FCSTD DOCUMENT  (FreeCAD 0.14R3700 (Git))
Label: 1
License: CC-BY 3.0
LicenseURL: http://creativecommons.org/licenses/by/3.0/
objects: Part::Part2DObjectPython×19
note: 19 computed .brp shape members not serialized (recipe doc carries the construction recipe); baked Part::Feature solids carry a one-line shape summary decoded from their .brp

FEATURE [Part::Part2DObjectPython] Circle  # Draft 2D object (typed FeaturePython)
  FirstAngle = 0
  LastAngle = 0
  MakeFace = false
  Placement = pos=(17,45,0) rot=(0,0,1;3.14159rad)
  Radius = 1.5
FEATURE [Part::Part2DObjectPython] Circle002  # Draft 2D object (typed FeaturePython)
  FirstAngle = 0
  LastAngle = 0
  MakeFace = false
  Placement = pos=(12.5,7,0) rot=(0,0,1;3.14159rad)
  Radius = 1.5
FEATURE [Part::Part2DObjectPython] Circle003  # Draft 2D object (typed FeaturePython)
  FirstAngle = 0
  LastAngle = 0
  MakeFace = false
  Placement = pos=(-17,45,0) rot=(0,0,1;3.14159rad)
  Radius = 1.5
FEATURE [Part::Part2DObjectPython] Circle004  # Draft 2D object (typed FeaturePython)
  FirstAngle = 0
  LastAngle = 0
  MakeFace = false
  Placement = pos=(-12.5,7,0) rot=(0,0,1;3.14159rad)
  Radius = 1.5
FEATURE [Part::Part2DObjectPython] Rectangle  # Draft 2D object (typed FeaturePython)
  ChamferSize = 0
  FilletRadius = 0
  Height = 60
  Length = 40
  MakeFace = false
  Placement = pos=(20,60,0) rot=(0,0,1;3.14159rad)
FEATURE [Part::Part2DObjectPython] Rectangle001  # Draft 2D object (typed FeaturePython)
  ChamferSize = 0
  FilletRadius = 0
  Height = 53.5
  Length = 66.5
  MakeFace = false
  Placement = pos=(27,0,0) rot=(0,0,1;1.5708rad)
FEATURE [Part::Part2DObjectPython] Circle005  # Draft 2D object (typed FeaturePython)
  FirstAngle = 0
  LastAngle = 0
  MakeFace = false
  Placement = pos=(-23.9,14.2,0) rot=(0,0,1;1.5708rad)
  Radius = 1.5
FEATURE [Part::Part2DObjectPython] Circle006  # Draft 2D object (typed FeaturePython)
  FirstAngle = 0
  LastAngle = 0
  MakeFace = false
  Placement = pos=(24.4,15.6,0) rot=(0,0,1;1.5708rad)
  Radius = 1.5
FEATURE [Part::Part2DObjectPython] Circle007  # Draft 2D object (typed FeaturePython)
  FirstAngle = 0
  LastAngle = 0
  MakeFace = false
  Placement = pos=(-19,66.5,0) rot=(0,0,1;1.5708rad)
  Radius = 1.5
FEATURE [Part::Part2DObjectPython] Rectangle002  # Draft 2D object (typed FeaturePython)
  ChamferSize = 0
  FilletRadius = 2
  Height = 72
  Length = 66
  MakeFace = false
  Placement = pos=(-33,0,0) rot=(0,0,1;0rad)
FEATURE [Part::Part2DObjectPython] Circle008  # Draft 2D object (typed FeaturePython)
  FirstAngle = 0
  LastAngle = 0
  MakeFace = false
  Placement = pos=(-30,3,0) rot=(0,0,1;0rad)
  Radius = 1.5
FEATURE [Part::Part2DObjectPython] Circle009  # Draft 2D object (typed FeaturePython)
  FirstAngle = 0
  LastAngle = 0
  MakeFace = false
  Placement = pos=(30,3,0) rot=(0,0,1;0rad)
  Radius = 1.5
FEATURE [Part::Part2DObjectPython] Circle010  # Draft 2D object (typed FeaturePython)
  FirstAngle = 0
  LastAngle = 0
  MakeFace = false
  Placement = pos=(-30,69,0) rot=(0,0,1;0rad)
  Radius = 1.5
FEATURE [Part::Part2DObjectPython] Circle011  # Draft 2D object (typed FeaturePython)
  FirstAngle = 0
  LastAngle = 0
  MakeFace = false
  Placement = pos=(30,69,0) rot=(0,0,1;0rad)
  Radius = 1.5
FEATURE [Part::Part2DObjectPython] Rectangle003  # Draft 2D object (typed FeaturePython)
  ChamferSize = 0
  FilletRadius = 2
  Height = 72
  Length = 66
  MakeFace = false
  Placement = pos=(35,0,0) rot=(0,0,1;0rad)
FEATURE [Part::Part2DObjectPython] Circle014  # Draft 2D object (typed FeaturePython)
  FirstAngle = 0
  LastAngle = 0
  MakeFace = false
  Placement = pos=(38,69,0) rot=(0,0,1;0rad)
  Radius = 1.5
FEATURE [Part::Part2DObjectPython] Circle012  # Draft 2D object (typed FeaturePython)
  FirstAngle = 0
  LastAngle = 0
  MakeFace = false
  Placement = pos=(98,69,0) rot=(0,0,1;0rad)
  Radius = 1.5
FEATURE [Part::Part2DObjectPython] Circle013  # Draft 2D object (typed FeaturePython)
  FirstAngle = 0
  LastAngle = 0
  MakeFace = false
  Placement = pos=(98,3,0) rot=(0,0,1;0rad)
  Radius = 1.5
FEATURE [Part::Part2DObjectPython] Circle015  # Draft 2D object (typed FeaturePython)
  FirstAngle = 0
  LastAngle = 0
  MakeFace = false
  Placement = pos=(38,3,0) rot=(0,0,1;0rad)
  Radius = 1.5
